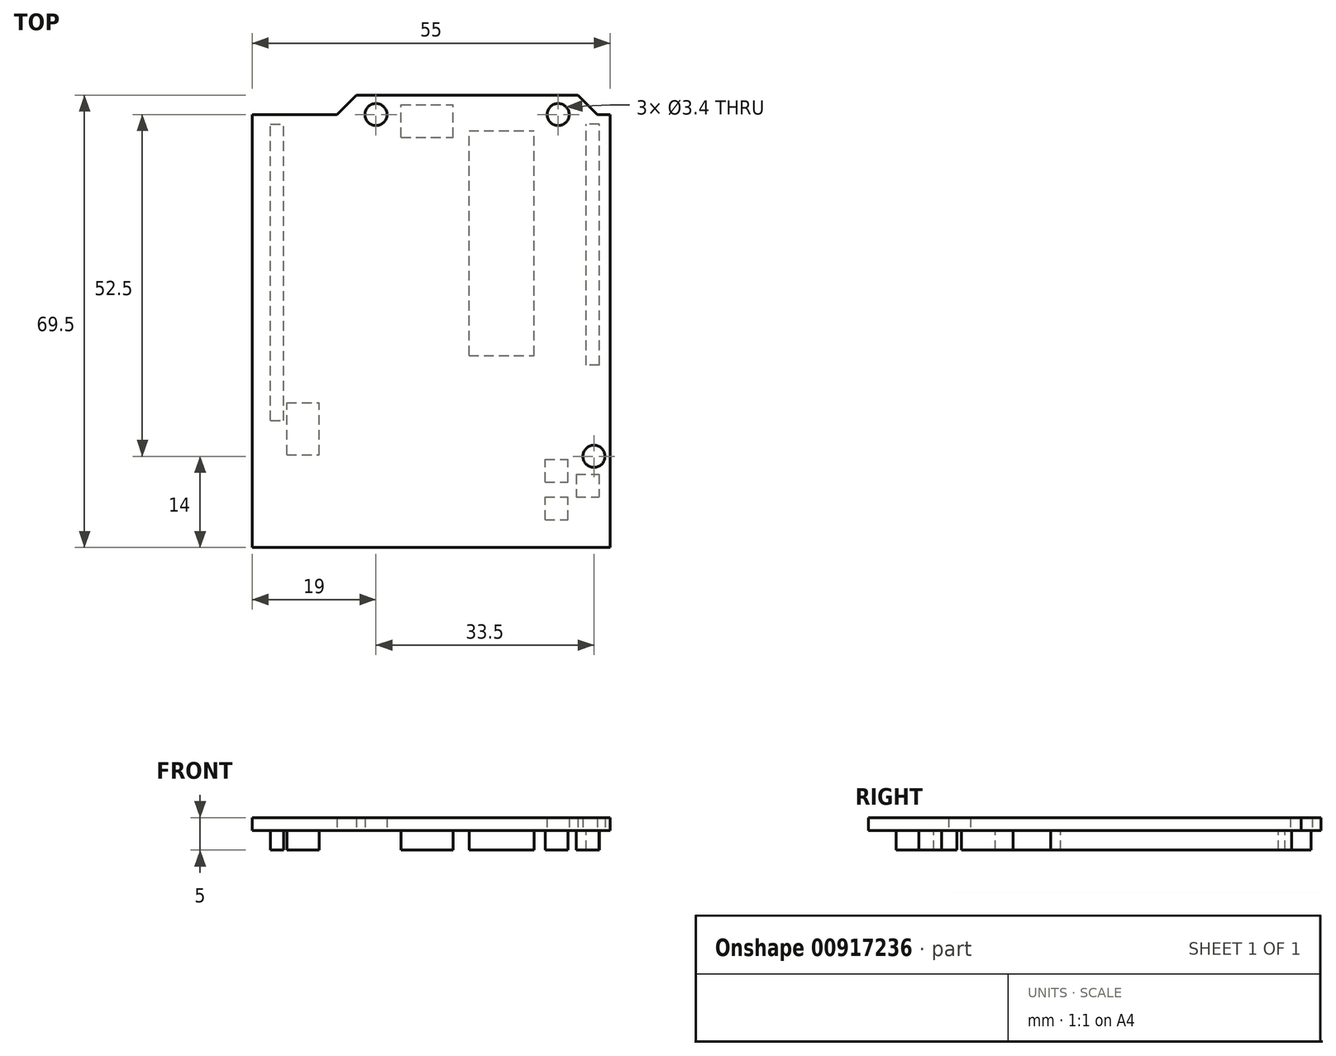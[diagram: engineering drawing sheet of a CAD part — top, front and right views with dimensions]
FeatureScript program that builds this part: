
annotation { "Feature Type Name" : "Feature", "Feature Type Description" : "" }
export const myFeature = defineFeature(function(context is Context, id is Id, definition is map)
    precondition{}
    {
        {
            var Q0;
            Q0=qCreatedBy(makeId("Top.planeOp"),FACE);
            var sketch = newSketch(context, id + "F0", { "sketchPlane" : qUnion([Q0])});
            skLineSegment(sketch, "E0", {"start": v(-27.5, -29.5) * mm, "end": v(-27.5, 37) * mm});
            skLineSegment(sketch, "E1", {"start": v(-27.5, 37) * mm, "end": v(-14.5, 37) * mm});
            skLineSegment(sketch, "E2", {"start": v(-14.5, 37) * mm, "end": v(-11.5, 40) * mm});
            skLineSegment(sketch, "E3", {"start": v(-11.5, 40) * mm, "end": v(22.5, 40) * mm});
            skLineSegment(sketch, "E4", {"start": v(22.5, 40) * mm, "end": v(25.5, 37) * mm});
            skLineSegment(sketch, "E5", {"start": v(25.5, 37) * mm, "end": v(27.5, 37) * mm});
            skLineSegment(sketch, "E6", {"start": v(27.5, 37) * mm, "end": v(27.5, -29.5) * mm});
            skLineSegment(sketch, "E7", {"start": v(27.5, -29.5) * mm, "end": v(-27.5, -29.5) * mm});
            skLineSegment(sketch, "E8", {"start": v(5.5, 36.96) * mm, "end": v(5.5, 26.44) * mm, "construction": true});
            skCircle(sketch, "E9", {"center": v(25, -15.5) * mm, "radius": 1.7 * mm});
            skCircle(sketch, "E10", {"center": v(-8.5, 37) * mm, "radius": 1.7 * mm});
            skCircle(sketch, "E11", {"center": v(19.5, 37) * mm, "radius": 1.7 * mm});
            skLineSegment(sketch, "E12", {"start": v(0, -29.5) * mm, "end": v(0, 40) * mm, "construction": true});
            skLineSegment(sketch, "E13", {"start": v(-8.5, 37) * mm, "end": v(19.5, 37) * mm, "construction": true});
            skSolve(sketch);
        }
        {
            var Q0;
            Q0=qSketchRegion(id+"F0",true);
            extrude(context, id + "F1", {"entities" : qUnion([Q0]), "depth" : 2 * mm, "offsetDistance" : 25 * mm});
        }
        {
            var Q0;
            {var subQ6=sQuery(id+"F0.wireOp",EDGE,"E1");Q0=makeQuery(id+"F0.imprint","IMPRINT",FACE,{"disambiguationData":[TD([[makeQuery(id+"F0.imprint","IMPRINT",EDGE,{"derivedFrom":subQ6}),-1.0]])]});}
            var sketch = newSketch(context, id + "F2", { "sketchPlane" : qUnion([Q0])});
            skLineSegment(sketch, "E14.bottom", {"start": v(-4.64, 33.5) * mm, "end": v(-4.64, 38.5) * mm});
            skLineSegment(sketch, "E14.top", {"start": v(3.36, 33.5) * mm, "end": v(3.36, 38.5) * mm});
            skLineSegment(sketch, "E14.left", {"start": v(-4.64, 33.5) * mm, "end": v(3.36, 33.5) * mm});
            skLineSegment(sketch, "E14.right", {"start": v(-4.64, 38.5) * mm, "end": v(3.36, 38.5) * mm});
            skLineSegment(sketch, "E15.bottom", {"start": v(5.81, 0) * mm, "end": v(5.8, 34.5) * mm});
            skLineSegment(sketch, "E15.top", {"start": v(15.8, 0) * mm, "end": v(15.8, 34.5) * mm});
            skLineSegment(sketch, "E15.left", {"start": v(5.81, 0) * mm, "end": v(15.8, 0) * mm});
            skLineSegment(sketch, "E15.right", {"start": v(5.8, 34.5) * mm, "end": v(15.8, 34.5) * mm});
            skLineSegment(sketch, "E16.bottom", {"start": v(-24.7, -10) * mm, "end": v(-24.7, 35.5) * mm});
            skLineSegment(sketch, "E16.top", {"start": v(-22.69, -10) * mm, "end": v(-22.7, 35.5) * mm});
            skLineSegment(sketch, "E16.left", {"start": v(-24.7, -10) * mm, "end": v(-22.69, -10) * mm});
            skLineSegment(sketch, "E16.right", {"start": v(-24.7, 35.5) * mm, "end": v(-22.7, 35.5) * mm});
            skLineSegment(sketch, "E17.bottom", {"start": v(25.81, -1.5) * mm, "end": v(25.8, 35.5) * mm});
            skLineSegment(sketch, "E17.top", {"start": v(23.8, -1.5) * mm, "end": v(23.8, 35.5) * mm});
            skLineSegment(sketch, "E17.left", {"start": v(25.81, -1.5) * mm, "end": v(23.8, -1.5) * mm});
            skLineSegment(sketch, "E17.right", {"start": v(25.8, 35.5) * mm, "end": v(23.8, 35.5) * mm});
            skLineSegment(sketch, "E18.bottom", {"start": v(-22.2, -15.25) * mm, "end": v(-22.2, -7.25) * mm});
            skLineSegment(sketch, "E18.top", {"start": v(-17.2, -15.25) * mm, "end": v(-17.2, -7.25) * mm});
            skLineSegment(sketch, "E18.left", {"start": v(-22.2, -15.25) * mm, "end": v(-17.2, -15.25) * mm});
            skLineSegment(sketch, "E18.right", {"start": v(-22.2, -7.25) * mm, "end": v(-17.2, -7.25) * mm});
            skLineSegment(sketch, "E19.bottom", {"start": v(17.5, -25.25) * mm, "end": v(17.5, -21.75) * mm});
            skLineSegment(sketch, "E19.top", {"start": v(21, -25.25) * mm, "end": v(21, -21.75) * mm});
            skLineSegment(sketch, "E19.left", {"start": v(17.5, -25.25) * mm, "end": v(21, -25.25) * mm});
            skLineSegment(sketch, "E19.right", {"start": v(17.5, -21.75) * mm, "end": v(21, -21.75) * mm});
            skLineSegment(sketch, "E20.bottom", {"start": v(17.5, -19.45) * mm, "end": v(17.5, -15.95) * mm});
            skLineSegment(sketch, "E20.top", {"start": v(21, -19.45) * mm, "end": v(21, -15.95) * mm});
            skLineSegment(sketch, "E20.left", {"start": v(17.5, -19.45) * mm, "end": v(21, -19.45) * mm});
            skLineSegment(sketch, "E20.right", {"start": v(17.5, -15.95) * mm, "end": v(21, -15.95) * mm});
            skLineSegment(sketch, "E21.bottom", {"start": v(22.25, -18.25) * mm, "end": v(22.25, -21.75) * mm});
            skLineSegment(sketch, "E21.top", {"start": v(25.75, -18.25) * mm, "end": v(25.75, -21.75) * mm});
            skLineSegment(sketch, "E21.left", {"start": v(22.25, -18.25) * mm, "end": v(25.75, -18.25) * mm});
            skLineSegment(sketch, "E21.right", {"start": v(22.25, -21.75) * mm, "end": v(25.75, -21.75) * mm});
            skSolve(sketch);
        }
        {
            var Q0;
            Q0=makeQuery(id+"F2.imprint","IMPRINT",FACE,{"disambiguationData":[TD([[makeQuery(id+"F2.imprint","IMPRINT",EDGE,{"derivedFrom":sQuery(id+"F2.wireOp",EDGE,"E18.bottom")}),-1.0]])]});
            var Q1;
            Q1=makeQuery(id+"F2.imprint","IMPRINT",FACE,{"disambiguationData":[TD([[makeQuery(id+"F2.imprint","IMPRINT",EDGE,{"derivedFrom":sQuery(id+"F2.wireOp",EDGE,"E20.bottom")}),-1.0]])]});
            var Q2;
            Q2=makeQuery(id+"F2.imprint","IMPRINT",FACE,{"disambiguationData":[TD([[makeQuery(id+"F2.imprint","IMPRINT",EDGE,{"derivedFrom":sQuery(id+"F2.wireOp",EDGE,"E21.bottom")}),1.0]])]});
            var Q3;
            Q3=makeQuery(id+"F2.imprint","IMPRINT",FACE,{"disambiguationData":[TD([[makeQuery(id+"F2.imprint","IMPRINT",EDGE,{"derivedFrom":sQuery(id+"F2.wireOp",EDGE,"E14.bottom")}),-1.0]])]});
            var Q4;
            {var subQ0=sQuery(id+"F2.wireOp",EDGE,"E15.left");Q4=makeQuery(id+"F2.imprint","IMPRINT",FACE,{"disambiguationData":[TD([[makeQuery(id+"F2.imprint","IMPRINT",EDGE,{"derivedFrom":subQ0}),1.0]])]});}
            var Q5;
            {var subQ0=sQuery(id+"F2.wireOp",EDGE,"E15.right");Q5=makeQuery(id+"F2.imprint","IMPRINT",FACE,{"disambiguationData":[TD([[makeQuery(id+"F2.imprint","IMPRINT",EDGE,{"derivedFrom":subQ0}),-1.0]])]});}
            var Q6;
            {var subQ9=sQuery(id+"F2.wireOp",EDGE,"E16.left");Q6=makeQuery(id+"F2.imprint","IMPRINT",FACE,{"disambiguationData":[TD([[makeQuery(id+"F2.imprint","IMPRINT",EDGE,{"derivedFrom":subQ9}),1.0]])]});}
            var Q7;
            {var subQ9=sQuery(id+"F2.wireOp",EDGE,"E17.left");Q7=makeQuery(id+"F2.imprint","IMPRINT",FACE,{"disambiguationData":[TD([[makeQuery(id+"F2.imprint","IMPRINT",EDGE,{"derivedFrom":subQ9}),-1.0]])]});}
            var Q8;
            {var subQ0=sQuery(id+"F2.wireOp",EDGE,"E16.right");Q8=makeQuery(id+"F2.imprint","IMPRINT",FACE,{"disambiguationData":[TD([[makeQuery(id+"F2.imprint","IMPRINT",EDGE,{"derivedFrom":subQ0}),-1.0]])]});}
            var Q9;
            {var subQ0=sQuery(id+"F2.wireOp",EDGE,"E17.right");Q9=makeQuery(id+"F2.imprint","IMPRINT",FACE,{"disambiguationData":[TD([[makeQuery(id+"F2.imprint","IMPRINT",EDGE,{"derivedFrom":subQ0}),1.0]])]});}
            var Q10;
            Q10=makeQuery(id+"F2.imprint","IMPRINT",FACE,{"disambiguationData":[TD([[makeQuery(id+"F2.imprint","IMPRINT",EDGE,{"derivedFrom":sQuery(id+"F2.wireOp",EDGE,"E19.bottom")}),-1.0]])]});
            extrude(context, id + "F3", {"entities" : qUnion([Q0, Q1, Q2, Q3, Q4, Q5, Q6, Q7, Q8, Q9, Q10]), "surfaceOperationType" : NewSurfaceOperationType.ADD, "oppositeDirection" : true, "depth" : 3 * mm, "offsetDistance" : 25 * mm});
        }
    });
